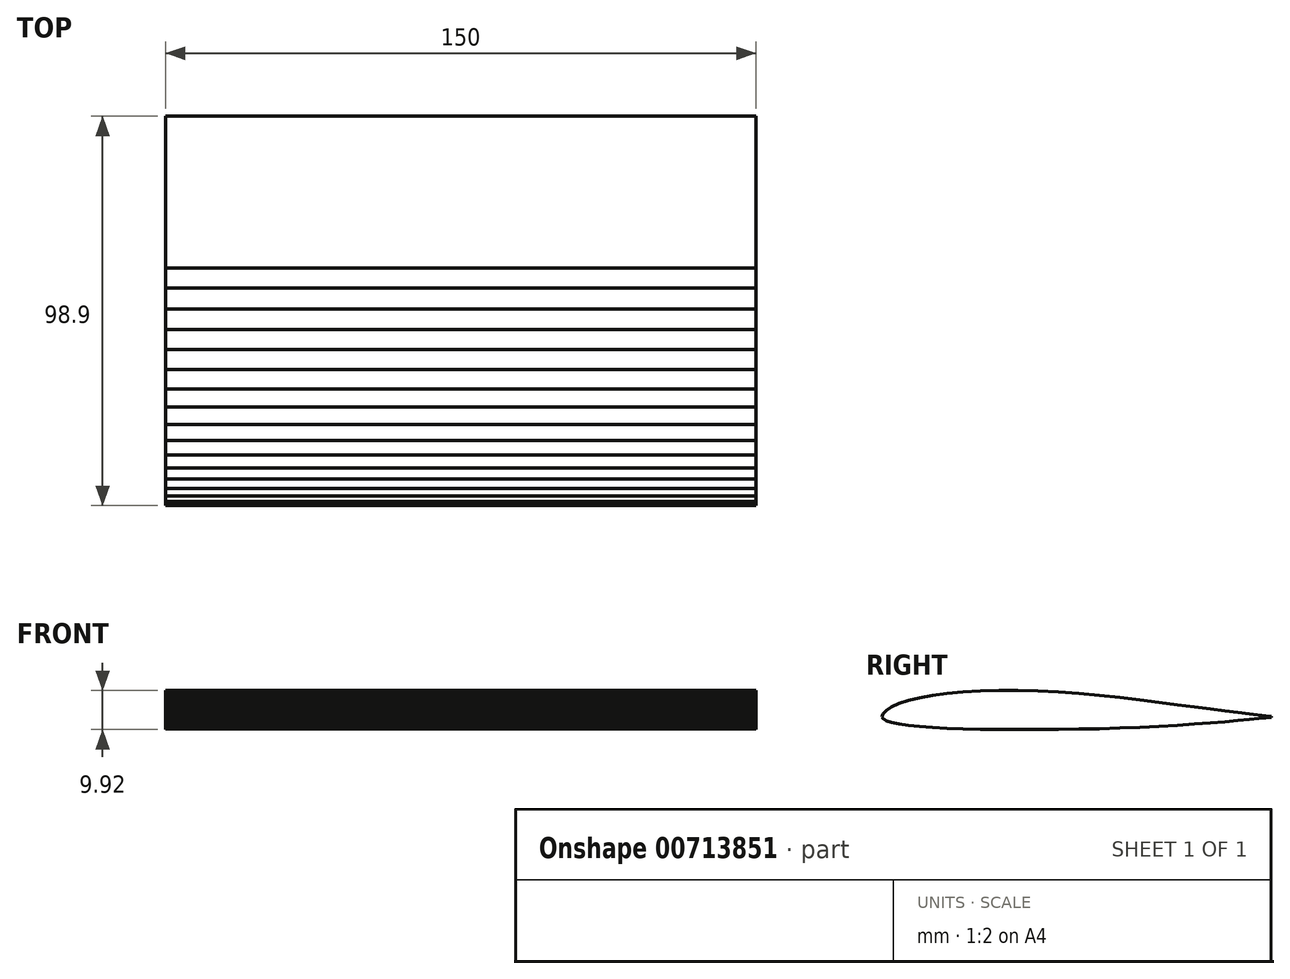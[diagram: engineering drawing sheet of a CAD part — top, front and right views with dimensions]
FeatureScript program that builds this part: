
annotation { "Feature Type Name" : "Feature", "Feature Type Description" : "" }
export const myFeature = defineFeature(function(context is Context, id is Id, definition is map)
    precondition{}
    {
        {
            var Q0;
            Q0=qCreatedBy(makeId("Right.planeOp"),FACE);
            var sketch = newSketch(context, id + "F0", { "sketchPlane" : qUnion([Q0])});
            skLineSegment(sketch, "E0", {"start": v(49.4, -1.59) * mm, "end": v(48.05, -1.44) * mm});
            skLineSegment(sketch, "E1", {"start": v(48.05, -1.44) * mm, "end": v(43.8, -0.95) * mm});
            skLineSegment(sketch, "E2", {"start": v(43.8, -0.95) * mm, "end": v(40.95, -0.6) * mm});
            skLineSegment(sketch, "E3", {"start": v(40.95, -0.6) * mm, "end": v(37.65, -0.2) * mm});
            skLineSegment(sketch, "E4", {"start": v(37.65, -0.2) * mm, "end": v(33.95, 0.27) * mm});
            skLineSegment(sketch, "E5", {"start": v(33.95, 0.27) * mm, "end": v(29.89, 0.79) * mm});
            skLineSegment(sketch, "E6", {"start": v(29.89, 0.79) * mm, "end": v(25.5, 1.36) * mm});
            skLineSegment(sketch, "E7", {"start": v(25.5, 1.36) * mm, "end": v(20.83, 1.96) * mm});
            skLineSegment(sketch, "E8", {"start": v(20.83, 1.96) * mm, "end": v(15.95, 2.56) * mm});
            skLineSegment(sketch, "E9", {"start": v(15.95, 2.56) * mm, "end": v(10.9, 3.15) * mm});
            skLineSegment(sketch, "E10", {"start": v(10.9, 3.15) * mm, "end": v(5.72, 3.7) * mm});
            skLineSegment(sketch, "E11", {"start": v(5.72, 3.7) * mm, "end": v(0.5, 4.17) * mm});
            skLineSegment(sketch, "E12", {"start": v(0.5, 4.17) * mm, "end": v(-4.73, 4.55) * mm});
            skLineSegment(sketch, "E13", {"start": v(-4.73, 4.55) * mm, "end": v(-9.9, 4.82) * mm});
            skLineSegment(sketch, "E14", {"start": v(-9.9, 4.82) * mm, "end": v(-14.95, 4.96) * mm});
            skLineSegment(sketch, "E15", {"start": v(-14.95, 4.96) * mm, "end": v(-19.84, 4.96) * mm});
            skLineSegment(sketch, "E16", {"start": v(-19.84, 4.96) * mm, "end": v(-24.5, 4.85) * mm});
            skLineSegment(sketch, "E17", {"start": v(-24.5, 4.85) * mm, "end": v(-28.9, 4.6) * mm});
            skLineSegment(sketch, "E18", {"start": v(-28.9, 4.6) * mm, "end": v(-32.96, 4.22) * mm});
            skLineSegment(sketch, "E19", {"start": v(-32.96, 4.22) * mm, "end": v(-36.66, 3.72) * mm});
            skLineSegment(sketch, "E20", {"start": v(-36.66, 3.72) * mm, "end": v(-39.95, 3.12) * mm});
            skLineSegment(sketch, "E21", {"start": v(-39.95, 3.12) * mm, "end": v(-42.8, 2.41) * mm});
            skLineSegment(sketch, "E22", {"start": v(-42.8, 2.41) * mm, "end": v(-45.18, 1.64) * mm});
            skLineSegment(sketch, "E23", {"start": v(-45.18, 1.64) * mm, "end": v(-47.06, 0.81) * mm});
            skLineSegment(sketch, "E24", {"start": v(-47.06, 0.81) * mm, "end": v(-48.4, -0.05) * mm});
            skLineSegment(sketch, "E25", {"start": v(-48.4, -0.05) * mm, "end": v(-49.23, -0.92) * mm});
            skLineSegment(sketch, "E26", {"start": v(-49.23, -0.92) * mm, "end": v(-49.5, -1.68) * mm});
            skLineSegment(sketch, "E27", {"start": v(-49.5, -1.68) * mm, "end": v(-49.23, -2.17) * mm});
            skLineSegment(sketch, "E28", {"start": v(-49.23, -2.17) * mm, "end": v(-48.4, -2.7) * mm});
            skLineSegment(sketch, "E29", {"start": v(-48.4, -2.7) * mm, "end": v(-47.06, -3.17) * mm});
            skLineSegment(sketch, "E30", {"start": v(-47.06, -3.17) * mm, "end": v(-45.18, -3.57) * mm});
            skLineSegment(sketch, "E31", {"start": v(-45.18, -3.57) * mm, "end": v(-42.8, -3.9) * mm});
            skLineSegment(sketch, "E32", {"start": v(-42.8, -3.9) * mm, "end": v(-39.95, -4.2) * mm});
            skLineSegment(sketch, "E33", {"start": v(-39.95, -4.2) * mm, "end": v(-36.66, -4.44) * mm});
            skLineSegment(sketch, "E34", {"start": v(-36.66, -4.44) * mm, "end": v(-32.96, -4.63) * mm});
            skLineSegment(sketch, "E35", {"start": v(-32.96, -4.63) * mm, "end": v(-28.9, -4.77) * mm});
            skLineSegment(sketch, "E36", {"start": v(-28.9, -4.77) * mm, "end": v(-24.5, -4.87) * mm});
            skLineSegment(sketch, "E37", {"start": v(-24.5, -4.87) * mm, "end": v(-19.84, -4.93) * mm});
            skLineSegment(sketch, "E38", {"start": v(-19.84, -4.93) * mm, "end": v(-14.95, -4.96) * mm});
            skLineSegment(sketch, "E39", {"start": v(-14.95, -4.96) * mm, "end": v(-9.9, -4.95) * mm});
            skLineSegment(sketch, "E40", {"start": v(-9.9, -4.95) * mm, "end": v(-4.73, -4.91) * mm});
            skLineSegment(sketch, "E41", {"start": v(-4.73, -4.91) * mm, "end": v(0.5, -4.84) * mm});
            skLineSegment(sketch, "E42", {"start": v(0.5, -4.84) * mm, "end": v(5.72, -4.72) * mm});
            skLineSegment(sketch, "E43", {"start": v(5.72, -4.72) * mm, "end": v(10.9, -4.57) * mm});
            skLineSegment(sketch, "E44", {"start": v(10.9, -4.57) * mm, "end": v(15.95, -4.37) * mm});
            skLineSegment(sketch, "E45", {"start": v(15.95, -4.37) * mm, "end": v(20.83, -4.14) * mm});
            skLineSegment(sketch, "E46", {"start": v(20.83, -4.14) * mm, "end": v(25.5, -3.87) * mm});
            skLineSegment(sketch, "E47", {"start": v(25.5, -3.87) * mm, "end": v(29.89, -3.58) * mm});
            skLineSegment(sketch, "E48", {"start": v(29.89, -3.58) * mm, "end": v(33.95, -3.26) * mm});
            skLineSegment(sketch, "E49", {"start": v(33.95, -3.26) * mm, "end": v(37.65, -2.95) * mm});
            skLineSegment(sketch, "E50", {"start": v(37.65, -2.95) * mm, "end": v(40.95, -2.65) * mm});
            skLineSegment(sketch, "E51", {"start": v(40.95, -2.65) * mm, "end": v(43.8, -2.37) * mm});
            skLineSegment(sketch, "E52", {"start": v(43.8, -2.37) * mm, "end": v(46.17, -2.12) * mm});
            skLineSegment(sketch, "E53", {"start": v(46.17, -2.12) * mm, "end": v(48.05, -1.94) * mm});
            skLineSegment(sketch, "E54", {"start": v(48.05, -1.94) * mm, "end": v(49.4, -1.81) * mm});
            skLineSegment(sketch, "E55", {"start": v(49.4, -1.81) * mm, "end": v(49.4, -1.59) * mm});
            skSolve(sketch);
        }
        {
            var Q0;
            Q0=makeQuery(id+"F0.imprint","IMPRINT",FACE,{"disambiguationData":[TD([[makeQuery(id+"F0.imprint","IMPRINT",EDGE,{"derivedFrom":sQuery(id+"F0.wireOp",EDGE,"E0")}),1.0]])]});
            extrude(context, id + "F1", {"entities" : qUnion([Q0]), "depth" : 150 * mm, "offsetDistance" : 25 * mm});
        }
    });
